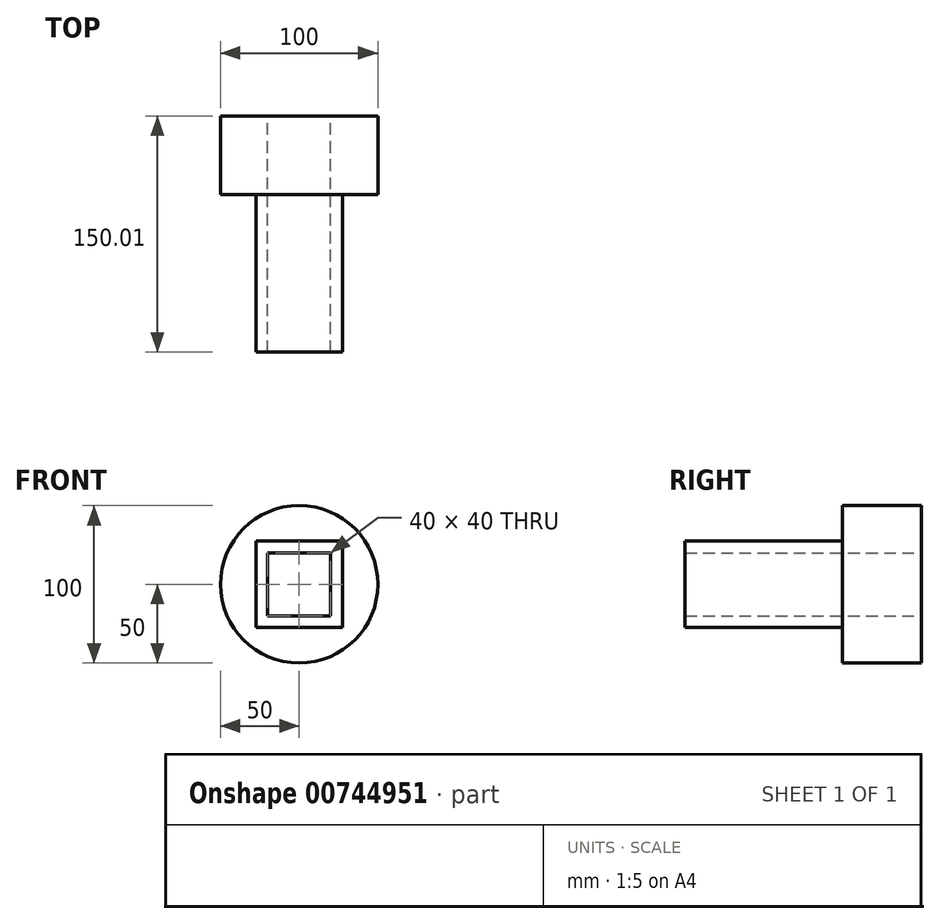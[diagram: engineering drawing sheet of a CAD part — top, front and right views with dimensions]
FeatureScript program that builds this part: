
annotation { "Feature Type Name" : "Feature", "Feature Type Description" : "" }
export const myFeature = defineFeature(function(context is Context, id is Id, definition is map)
    precondition{}
    {
        {
            var Q0;
            Q0=qCreatedBy(makeId("Front.planeOp"),FACE);
            var sketch = newSketch(context, id + "F0", { "sketchPlane" : qUnion([Q0])});
            skCircle(sketch, "E0", {"center": v(0, 0) * mm, "radius": 50 * mm});
            skLineSegment(sketch, "E1.bottom", {"start": v(-20, 20) * mm, "end": v(20, 20) * mm});
            skLineSegment(sketch, "E1.top", {"start": v(-20, -20) * mm, "end": v(20, -20) * mm});
            skLineSegment(sketch, "E1.left", {"start": v(-20, 20) * mm, "end": v(-20, -20) * mm});
            skLineSegment(sketch, "E1.right", {"start": v(20, 20) * mm, "end": v(20, -20) * mm});
            skLineSegment(sketch, "E2.bottom", {"start": v(-27.5, 27.5) * mm, "end": v(27.5, 27.5) * mm});
            skLineSegment(sketch, "E2.top", {"start": v(-27.5, -27.5) * mm, "end": v(27.5, -27.5) * mm});
            skLineSegment(sketch, "E2.left", {"start": v(-27.5, 27.5) * mm, "end": v(-27.5, -27.5) * mm});
            skLineSegment(sketch, "E2.right", {"start": v(27.5, 27.5) * mm, "end": v(27.5, -27.5) * mm});
            skSolve(sketch);
        }
        {
            var Q0;
            Q0=makeQuery(id+"F0.imprint","IMPRINT",FACE,{"disambiguationData":[TD([[makeQuery(id+"F0.imprint","IMPRINT",EDGE,{"derivedFrom":sQuery(id+"F0.wireOp",EDGE,"E1.bottom")}),1.0]])]});
            var Q1;
            Q1=makeQuery(id+"F0.imprint","IMPRINT",FACE,{"disambiguationData":[TD([[makeQuery(id+"F0.imprint","IMPRINT",EDGE,{"derivedFrom":sQuery(id+"F0.wireOp",EDGE,"E0")}),1.0]])]});
            extrude(context, id + "F1", {"entities" : qUnion([Q0, Q1]), "depth" : 50 * mm, "offsetDistance" : 25 * mm});
        }
        {
            var Q0;
            Q0=makeQuery(id+"F0.imprint","IMPRINT",FACE,{"disambiguationData":[TD([[makeQuery(id+"F0.imprint","IMPRINT",EDGE,{"derivedFrom":sQuery(id+"F0.wireOp",EDGE,"E1.bottom")}),1.0]])]});
            extrude(context, id + "F2", {"entities" : qUnion([Q0]), "operationType" : NewBodyOperationType.ADD, "endBound" : BoundingType.THROUGH_ALL, "depth" : 5 * mm, "offsetDistance" : 25 * mm});
        }
    });
